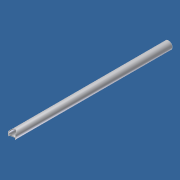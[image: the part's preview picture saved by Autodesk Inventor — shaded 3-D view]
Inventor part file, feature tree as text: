
AUTODESK INVENTOR PART (.ipt)
format: ipt  version: 2012 (Build 160160000, 160)  size: 91,648 bytes
history: native  units: in
note: dims shown in document units (in); Inventor stores cm internally (conversion verified against a paired STEP export)
features: other x4, sketch x2
ambient origin geometry x8: Origin, YZ Plane, XZ Plane, XY Plane, X Axis, Y Axis, Z Axis, Center Point
bodies: Solid1 (feature_tree)
feature tree (6):
  other  "GE-12057-01.ipt"
  other  "Solid1::GE-12057-01.ipt"
  sketch  "Sketch1"  dims[d0=0.3937in]
  sketch  "Sketch2"
  other  "Work Axis1"
  other  "TaggingFeature1"
